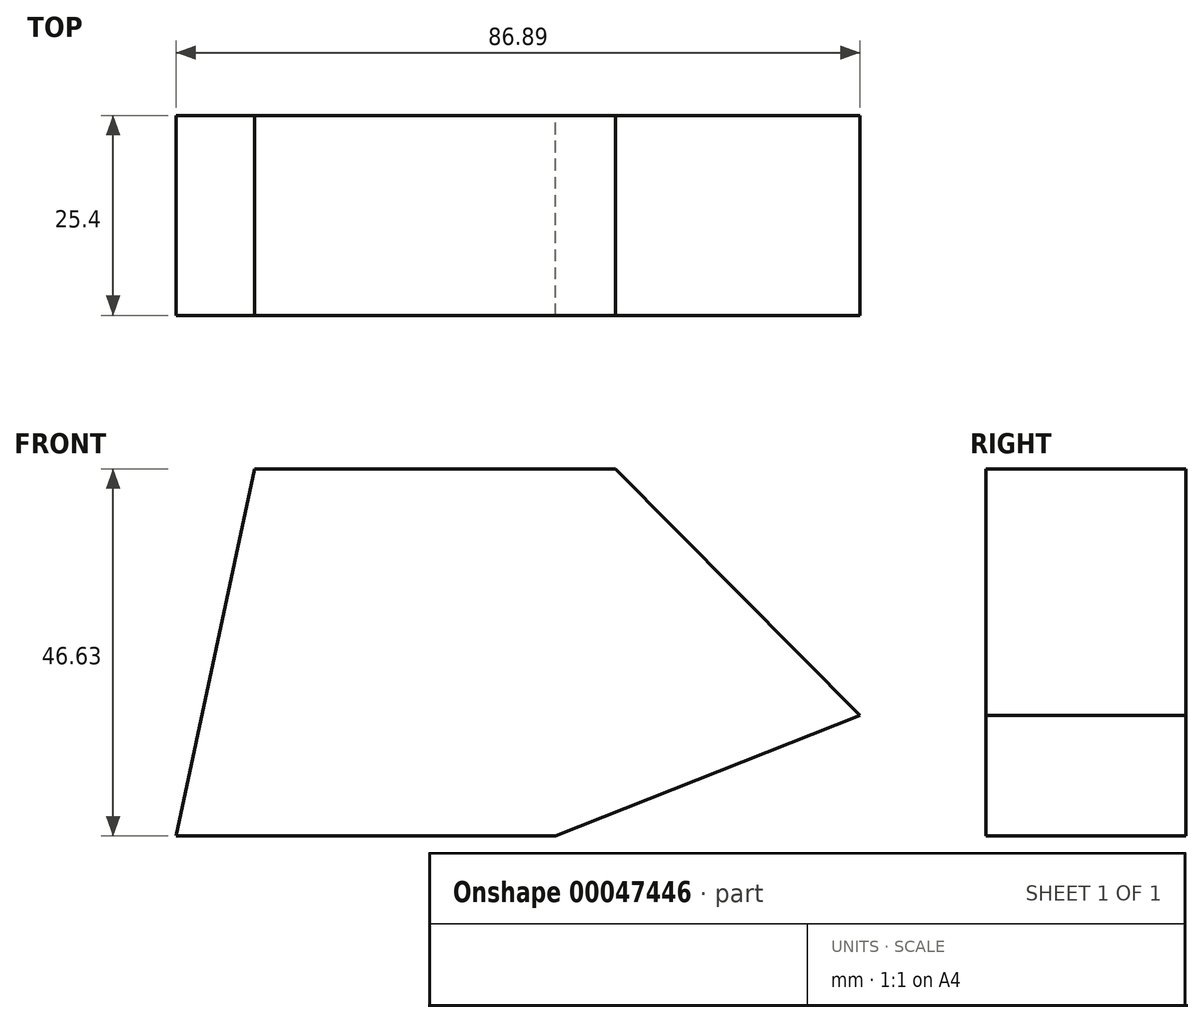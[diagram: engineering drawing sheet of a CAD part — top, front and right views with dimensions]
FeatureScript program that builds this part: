
annotation { "Feature Type Name" : "Feature", "Feature Type Description" : "" }
export const myFeature = defineFeature(function(context is Context, id is Id, definition is map)
    precondition{}
    {
        {
            var Q0;
            Q0=qCreatedBy(makeId("Front.planeOp"),FACE);
            var sketch = newSketch(context, id + "F0", { "sketchPlane" : qUnion([Q0])});
            skLineSegment(sketch, "E0", {"start": v(0, 0) * mm, "end": v(-48.16, 0) * mm});
            skLineSegment(sketch, "E1", {"start": v(-48.16, 0) * mm, "end": v(-38.22, 46.63) * mm});
            skLineSegment(sketch, "E2", {"start": v(-38.22, 46.63) * mm, "end": v(7.64, 46.63) * mm});
            skLineSegment(sketch, "E3", {"start": v(7.64, 46.63) * mm, "end": v(38.73, 15.29) * mm});
            skLineSegment(sketch, "E4", {"start": v(38.73, 15.29) * mm, "end": v(0, 0) * mm});
            skSolve(sketch);
        }
        {
            var Q0;
            Q0 = qSketchRegion(id + "F0", true);
            extrude(context, id + "F1", {"entities" : qUnion([Q0]), "depth" : 25.4 * mm, "offsetDistance" : 25.4 * mm});
        }
    });
